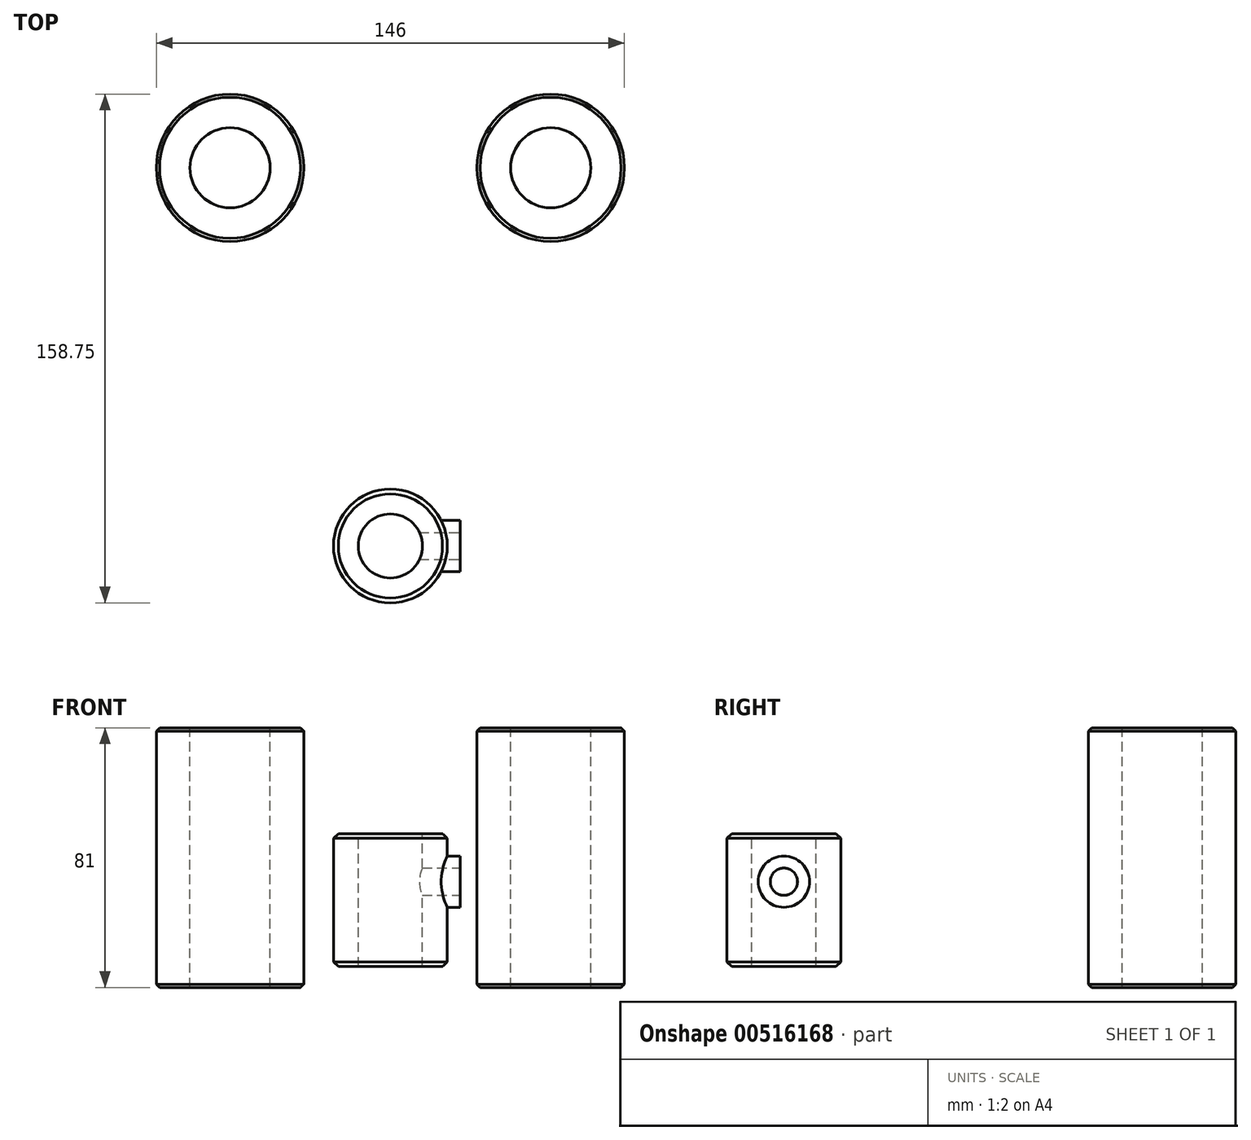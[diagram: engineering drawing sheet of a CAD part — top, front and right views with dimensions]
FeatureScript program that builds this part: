
annotation { "Feature Type Name" : "Feature", "Feature Type Description" : "" }
export const myFeature = defineFeature(function(context is Context, id is Id, definition is map)
    precondition{}
    {
        {
            var Q0;
            Q0=qCreatedBy(makeId("Top.planeOp"),FACE);
            var sketch = newSketch(context, id + "F0", { "sketchPlane" : qUnion([Q0])});
            skCircle(sketch, "E0", {"center": v(0, 0) * mm, "radius": 17.75 * mm});
            skSolve(sketch);
        }
        {
            var Q0;
            Q0=makeQuery(id+"F0.imprint","IMPRINT",FACE,{"disambiguationData":[TD([[makeQuery(id+"F0.imprint","IMPRINT",EDGE,{"derivedFrom":sQuery(id+"F0.wireOp",EDGE,"E0")}),1.0]])]});
            extrude(context, id + "F1", {"entities" : qUnion([Q0]), "depth" : 41.5 * mm, "offsetDistance" : 25 * mm});
        }
        {
            var Q0;
            Q0=makeQuery(id+"F1.opExtrude","CAP_FACE",FACE,{"disambiguationData":[OSD([sQuery(id+"F0.wireOp",EDGE,"E0")])],"isStart":false});
            var sketch = newSketch(context, id + "F2", { "sketchPlane" : qUnion([Q0])});
            skCircle(sketch, "E1", {"center": v(0, 0) * mm, "radius": 10 * mm});
            skSolve(sketch);
        }
        {
            var Q0;
            Q0 = qSketchRegion(id + "F2", true);
            extrude(context, id + "F3", {"entities" : qUnion([Q0]), "operationType" : NewBodyOperationType.REMOVE, "oppositeDirection" : true, "depth" : 42 * mm, "offsetDistance" : 25 * mm});
        }
        {
            var Q0;
            Q0=makeQuery(id+"F1.opExtrude","CAP_EDGE",EDGE,{"disambiguationData":[OSD([sQuery(id+"F0.wireOp",EDGE,"E0")])],"isStart":false});
            var Q1;
            Q1=makeQuery(id+"F1.opExtrude","CAP_EDGE",EDGE,{"disambiguationData":[OSD([sQuery(id+"F0.wireOp",EDGE,"E0")])],"isStart":true});
            chamfer(context, id + "F4", {"entities" : qUnion([Q0, Q1]), "width" : 1.5 * mm, "tangentPropagation" : true});
        }
        {
            var Q0;
            Q0=qCreatedBy(makeId("Top.planeOp"),FACE);
            cPlane(context, id + "F5", {"entities" : qUnion([Q0]), "cplaneType" : CPlaneType.OFFSET, "offset" : 26.5 * mm, "width" : 150 * mm, "height" : 150 * mm});
        }
        {
            var Q0;
            Q0=qCreatedBy(makeId("Right.planeOp"),FACE);
            cPlane(context, id + "F6", {"entities" : qUnion([Q0]), "cplaneType" : CPlaneType.OFFSET, "offset" : 17.75 * mm, "width" : 150 * mm, "height" : 150 * mm});
        }
        {
            var Q0;
            Q0=qCreatedBy(id+"F6.planeOp",FACE);
            var sketch = newSketch(context, id + "F7", { "sketchPlane" : qUnion([Q0])});
            skLineSegment(sketch, "E2", {"start": v(0, 0) * mm, "end": v(0, 26.5) * mm});
            skSolve(sketch);
        }
        {
            var Q0;
            Q0=qCreatedBy(makeId("Right.planeOp"),FACE);
            cPlane(context, id + "F8", {"entities" : qUnion([Q0]), "cplaneType" : CPlaneType.OFFSET, "offset" : 21.8 * mm, "width" : 150 * mm, "height" : 150 * mm});
        }
        {
            var Q0;
            Q0=qCreatedBy(id+"F8.planeOp",FACE);
            var sketch = newSketch(context, id + "F9", { "sketchPlane" : qUnion([Q0])});
            skCircle(sketch, "E3", {"center": v(0, 26.5) * mm, "radius": 8 * mm});
            skSolve(sketch);
        }
        {
            var Q0;
            Q0=makeQuery(id+"F9.imprint","IMPRINT",FACE,{"disambiguationData":[TD([[makeQuery(id+"F9.imprint","IMPRINT",EDGE,{"derivedFrom":sQuery(id+"F9.wireOp",EDGE,"E3")}),1.0]])]});
            extrude(context, id + "F10", {"entities" : qUnion([Q0]), "operationType" : NewBodyOperationType.ADD, "oppositeDirection" : true, "depth" : 7.2 * mm, "offsetDistance" : 25 * mm});
        }
        {
            var Q0;
            Q0=makeQuery(id+"F10.opExtrude","CAP_FACE",FACE,{"disambiguationData":[OSD([sQuery(id+"F9.wireOp",EDGE,"E3")])],"isStart":true});
            var sketch = newSketch(context, id + "F11", { "sketchPlane" : qUnion([Q0])});
            skLineSegment(sketch, "E4", {"start": v(0, 26.5) * mm, "end": v(0, 18.5) * mm});
            skSolve(sketch);
        }
        {
            var Q0;
            Q0=sQuery(id+"F11.wireOp",VERTEX,"E4.start");
            var Q1;
            Q1=makeQuery(id+"F1.opExtrude","SWEPT_BODY",BODY,{"disambiguationData":[OSD([sQuery(id+"F0.wireOp",EDGE,"E0")])]});
            hole(context, id + "F12", {"style" : HoleStyle.SIMPLE, "endStyle" : HoleEndStyle.BLIND, "standardTappedOrClearance" : lookupTablePath({ "standard" : "ISO", "engagement" : "75%", "pitch" : "1.5 mm", "size" : "M10", "type" : "Tapped" }), "standardBlindInLast" : lookupTablePath({ "standard" : "ISO", "engagement" : "75%", "pitch" : "1.5 mm", "size" : "M10", "type" : "Tapped" }), "holeDiameter" : 8.5 * mm, "showTappedDepth" : true, "holeDepth" : 16.5 * mm, "isTappedThrough" : true, "tappedDepth" : 12 * mm, "tapClearance" : 3, "locations" : qUnion([Q0]), "scope" : qUnion([Q1]), "majorDiameter" : 10 * mm});
        }
        {
            var Q0;
            Q0=qCreatedBy(makeId("Top.planeOp"),FACE);
            var sketch = newSketch(context, id + "F13", { "sketchPlane" : qUnion([Q0])});
            skLineSegment(sketch, "E5", {"start": v(0, 0) * mm, "end": v(0, 118) * mm});
            skLineSegment(sketch, "E6", {"start": v(0, 118) * mm, "end": v(50, 118) * mm});
            skLineSegment(sketch, "E7", {"start": v(0, 118) * mm, "end": v(-50, 118) * mm});
            skCircle(sketch, "E8", {"center": v(-50, 118) * mm, "radius": 23 * mm});
            skCircle(sketch, "E9", {"center": v(50, 118) * mm, "radius": 23 * mm});
            skSolve(sketch);
        }
        {
            var Q0;
            Q0=makeQuery(id+"F13.imprint","IMPRINT",FACE,{"disambiguationData":[TD([[makeQuery(id+"F13.imprint","IMPRINT",EDGE,{"derivedFrom":sQuery(id+"F13.wireOp",EDGE,"E8")}),1.0]])]});
            var Q1;
            Q1=makeQuery(id+"F13.imprint","IMPRINT",FACE,{"disambiguationData":[TD([[makeQuery(id+"F13.imprint","IMPRINT",EDGE,{"derivedFrom":sQuery(id+"F13.wireOp",EDGE,"E9")}),1.0]])]});
            extrude(context, id + "F14", {"entities" : qUnion([Q0, Q1]), "depth" : 74.5 * mm, "offsetDistance" : 25 * mm, "hasSecondDirection" : true, "secondDirectionOppositeDirection" : true, "secondDirectionDepth" : 6.5 * mm});
        }
        {
            var Q0;
            Q0=makeQuery(id+"F14.opExtrude","CAP_EDGE",EDGE,{"disambiguationData":[OSD([sQuery(id+"F13.wireOp",EDGE,"E8")])],"isStart":false});
            var Q1;
            Q1=makeQuery(id+"F14.opExtrude","CAP_EDGE",EDGE,{"disambiguationData":[OSD([sQuery(id+"F13.wireOp",EDGE,"E9")])],"isStart":false});
            var Q2;
            Q2=makeQuery(id+"F14.opExtrude","CAP_EDGE",EDGE,{"disambiguationData":[OSD([sQuery(id+"F13.wireOp",EDGE,"E9")])],"isStart":true});
            var Q3;
            Q3=makeQuery(id+"F14.opExtrude","CAP_EDGE",EDGE,{"disambiguationData":[OSD([sQuery(id+"F13.wireOp",EDGE,"E8")])],"isStart":true});
            chamfer(context, id + "F15", {"entities" : qUnion([Q0, Q1, Q2, Q3]), "width" : 1 * mm, "tangentPropagation" : true});
        }
        {
            var Q0;
            Q0=makeQuery(id+"F14.opExtrude","CAP_FACE",FACE,{"disambiguationData":[OSD([sQuery(id+"F13.wireOp",EDGE,"E8")])],"isStart":false});
            var sketch = newSketch(context, id + "F16", { "sketchPlane" : qUnion([Q0])});
            skCircle(sketch, "E10", {"center": v(-50, 118) * mm, "radius": 12.5 * mm});
            skSolve(sketch);
        }
        {
            var Q0;
            Q0=makeQuery(id+"F14.opExtrude","CAP_FACE",FACE,{"disambiguationData":[OSD([sQuery(id+"F13.wireOp",EDGE,"E9")])],"isStart":false});
            var sketch = newSketch(context, id + "F17", { "sketchPlane" : qUnion([Q0])});
            skCircle(sketch, "E11", {"center": v(50, 118) * mm, "radius": 12.5 * mm});
            skSolve(sketch);
        }
        {
            var Q0;
            Q0=makeQuery(id+"F16.imprint","IMPRINT",FACE,{"disambiguationData":[TD([[makeQuery(id+"F16.imprint","IMPRINT",EDGE,{"derivedFrom":sQuery(id+"F16.wireOp",EDGE,"E10")}),1.0]])]});
            var Q1;
            Q1=makeQuery(id+"F17.imprint","IMPRINT",FACE,{"disambiguationData":[TD([[makeQuery(id+"F17.imprint","IMPRINT",EDGE,{"derivedFrom":sQuery(id+"F17.wireOp",EDGE,"E11")}),1.0]])]});
            extrude(context, id + "F18", {"entities" : qUnion([Q0, Q1]), "operationType" : NewBodyOperationType.REMOVE, "oppositeDirection" : true, "depth" : 81 * mm, "offsetDistance" : 25 * mm});
        }
        {
            var Q0;
            Q0=makeQuery(id+"F17.imprint","IMPRINT",FACE,{"disambiguationData":[TD([[makeQuery(id+"F17.imprint","IMPRINT",EDGE,{"derivedFrom":sQuery(id+"F17.wireOp",EDGE,"E11")}),1.0]])]});
            extrude(context, id + "F19", {"entities" : qUnion([Q0]), "operationType" : NewBodyOperationType.REMOVE, "oppositeDirection" : true, "depth" : 81 * mm, "offsetDistance" : 25 * mm});
        }
    });
